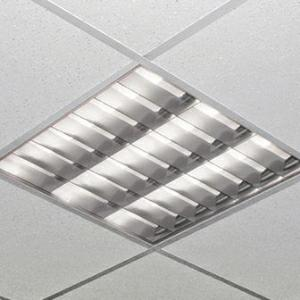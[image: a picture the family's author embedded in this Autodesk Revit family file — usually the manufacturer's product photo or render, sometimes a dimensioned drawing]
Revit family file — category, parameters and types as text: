
# Revit family: 3f_filippi_-_l_320_2mg_3f_filippi_-_28847_-_l_323x10w_led_ep_2mg_596x596
name_source: partatom
category: Lighting Fixtures
units: mm (PartAtom-declared; Revit-internal decimal feet)

## family parameters
Cut with Voids When Loaded = No
Host = Face
Light Source = No
Part Type = Normal
Room Calculation Point = No
Round Connector Dimension = Use Diameter
Shared = No

## types (1)
- 3F Filippi - L 320 2MG (1 x LED, 4287 lm, 35 W, 4000 K)
    Apparent Load = 35 VA
    Approval mark = ENEC
    CIE Flux Codes = 71 98 100 100 100
    Color Rendering = 80
    Color Temperature = 4000 K
    Control Gear = Electronic ballast
    Default Elevation = 1800 mm
    Description = ILLUMINOTECHNICAL
Luminous efficiency 100% (DLOR 100%, ULOR 0%).
Initial luminous flux of the luminaire 4287 lm.
Emergency luminaire luminous flux BLF 11.4%.
Direct symmetric distribution.
Installation Interdistance Transv.D = 1.27 x hu - Long.D = 1.17 x hu.
Average luminance <1000 cd/m² for radial angles >65°.
Tabular UGR (CIE 117 - 4H-8H; S=0.25H; 70/50/20): RUG 15.1 - 15.5.
Beam angle: 87° - 88°.
Luminous efficacy 122 lm/W.
Lifetime (L93/B10): 30000 h. (tq+25°C)
Lifetime (L90/B10): 50000 h. (tq+25°C)
Lifetime (L85/B10): 80000 h. (tq+25°C)
Lifetime (L80/B10): 100000 h. (tq+25°C)
Sudden decreased luminous flux after 50000 hours: 0% (C0).
Photobiological safety in compliance with IEC/TR 62778: RG0 risk exempt, (IEC 62471).
In compliance with IEC/EN 62722-2-1 - IEC/EN 62717 standards.

SOURCE
3 linear LED modules 10W/840.
Energy efficiency class (UE 2019/2020 - UE 2019/2015): D.
CIE 13.3 Colour rendering index: CRI >80 (R9 <50%).
IES TM-30 Fidelity Index: Rf = 84 Rg = 95.
CCT nominal colour temperature 4000 K.
Colour initial tolerance (MacAdam): SDCM 2.

MECHANICAL
Housing in hot-galvanised steel, painted in white polyester.
2MG parabolic louvre, high efficiency, in specular aluminium with superficial titanium-magnesium treatment, non-iridescent, with transverse blades closed at the top.
Prismatic flat diffusers in transparent methacrylate (PMMA), multilenticular, anti-glare, prismatic outer surface, positioned above the louvre blades.
Film protective against dust and finger marks, adhesive, attached to louvre.
Luminaire with limited surface temperature. - D - (EN 60598-2-24)
Dimensions: 596x596 mm, height 80 mm. Weight 4.75 kg.
IP20 protection degree.
Mechanical strength to impacts IK02 (0.2 joule).
Glow-wire test resistance 650°C.

ELECTRICAL
Halogen Free electronic wiring 230V-50/60Hz, power factor 0.85, THD <25%, constant output current, SELV, class I, 1 driver.
Power of the luminaire 35 W.
CE - IEC 60598-1 - EN 60598-1.
EP maintained emergency wiring on board, 1h duration, 24h recharge; compliant with EN 60598-2-22, excluding high risk areas.
SAFE FLICKER: PstLM=<1 and SVM=<0.4 (IEC TR 61547-1 and IEC TR 63158), to ensure a more comfortable and safe light.
Ambient temperature from +5°C to +25°C.
Temperature class T6 max 85°C.
Relative humidity UR: <85%.

INSTALLATION
Lay-in recessed fitting.
On request: pull-up recessed fitting with brackets.
False ceiling carving: 580x580 mm.
All accessories dedicated to this product are available on the Catalog and on our website www.3F-Filippi.com.

APPLICATIONS
In environments with VDTs, managerial offices and staterooms, public offices and schools.

WARNING
Luminaire designed for disposal/recycling at end-of-life.
Replaceable (LED only) light source by a professional. Replaceable control gear by a professional.
    Height = 0 mm  [stored 0 ft]
    Lamp = 1 x LED
    Lamp Light Flux = 4287 lm
    Lamp Power = 35 W
    Lamp count = 1
    Length = 596 mm
    Lifetime = 50000 h
    Luminous efficacy = 122 lm/W
    Manufacturer = 3F Filippi
    ModVariant = No
    Model = 3F Filippi - 28847 - L 323x10W LED EP 2MG 596x596
    Mounting Place = Ceiling
    Mounting Type = Recessed
    Number of Poles = 1
    OnlyDefault = Yes
    Power Factor = 1
    Product Name = 3F Filippi - L 320 2MG
    Product group = recessed luminaire
    ProductGroupID = 4
    Protection Class = Protection class I
    Protection Degree = IP 20
    RLX_Detail_Level = 1
    RLX_Emergency_Light_Flux = 0 lm
    RLX_Emergency_Type = 0
    RLX_Emergency_Type_DB = No
    RlxData = <blob elided: 92841 chars, md5=c27d2230>
    Socket = socket
    Standby Power = 0 W
    System Light Flux = 4287 lm
    System Power = 35 W
    Type Comments = Product without accessories
    Type Image = 3ffilippi_28847.jpg
    URL = http://relux.com
    VarID = ---
    Voltage = 0 V
    Weight = 0.00 kg
    Width = 596 mm

note: [stored X ft] marks values corroborated as IEEE doubles in the binary element streams (Revit-internal decimal feet)

## geometry (parser evidence)
native form markers: Blend x4, Sweep x11
no freeform markers — native parametric forms only
